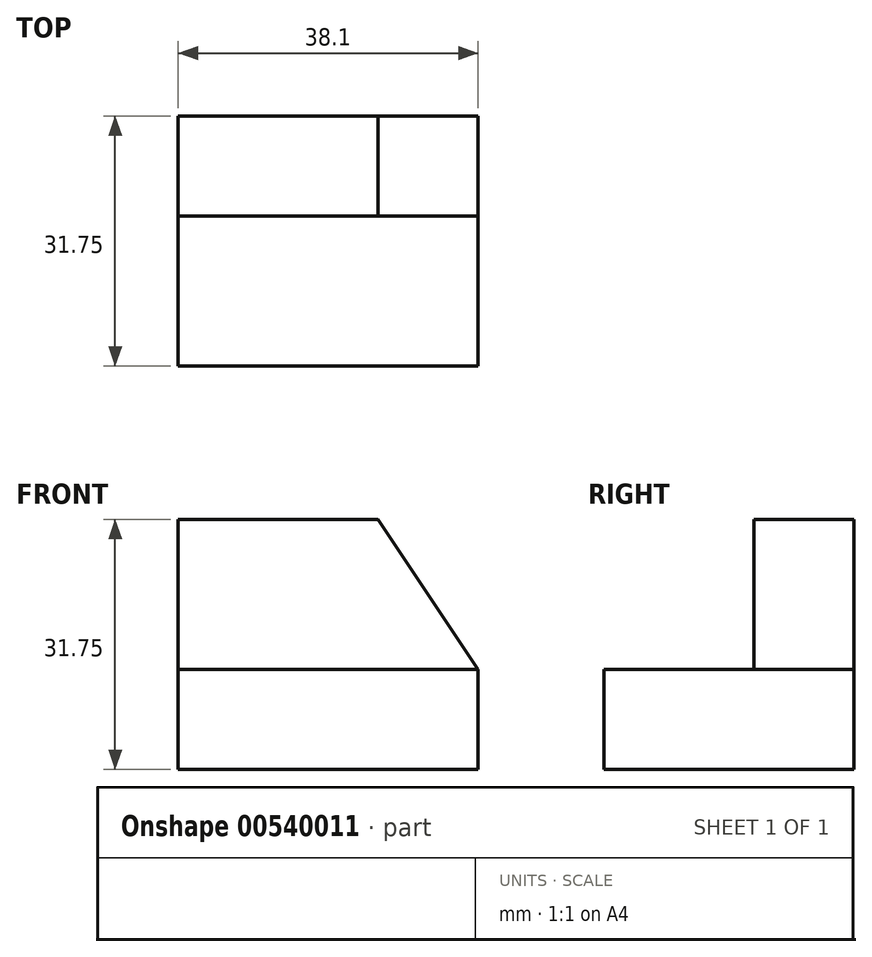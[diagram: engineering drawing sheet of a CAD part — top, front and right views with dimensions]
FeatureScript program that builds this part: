
annotation { "Feature Type Name" : "Feature", "Feature Type Description" : "" }
export const myFeature = defineFeature(function(context is Context, id is Id, definition is map)
    precondition{}
    {
        {
            var Q0;
            Q0=qCreatedBy(makeId("Right.planeOp"),FACE);
            var sketch = newSketch(context, id + "F0", { "sketchPlane" : qUnion([Q0])});
            skLineSegment(sketch, "E0", {"start": v(-47.28, 42.2) * mm, "end": v(-34.58, 42.2) * mm});
            skLineSegment(sketch, "E1", {"start": v(-47.28, 42.2) * mm, "end": v(-47.28, 23.16) * mm});
            skLineSegment(sketch, "E2", {"start": v(-47.28, 23.16) * mm, "end": v(-66.33, 23.16) * mm});
            skLineSegment(sketch, "E3", {"start": v(-66.33, 23.16) * mm, "end": v(-66.33, 10.46) * mm});
            skLineSegment(sketch, "E4", {"start": v(-66.33, 10.46) * mm, "end": v(-34.58, 10.46) * mm});
            skLineSegment(sketch, "E5", {"start": v(-34.58, 42.2) * mm, "end": v(-34.58, 10.46) * mm});
            skSolve(sketch);
        }
        {
            var Q0;
            Q0=makeQuery(id+"F0.imprint","IMPRINT",FACE,{"disambiguationData":[TD([[makeQuery(id+"F0.imprint","IMPRINT",EDGE,{"derivedFrom":sQuery(id+"F0.wireOp",EDGE,"E0")}),-1.0]])]});
            extrude(context, id + "F1", {"entities" : qUnion([Q0]), "depth" : 38.1 * mm, "offsetDistance" : 25.4 * mm});
        }
        {
            var Q0;
            Q0=makeQuery(id+"F1.opExtrude","SWEPT_FACE",FACE,{"disambiguationData":[OSD([sQuery(id+"F0.wireOp",EDGE,"E1")])]});
            var sketch = newSketch(context, id + "F2", { "sketchPlane" : qUnion([Q0])});
            skLineSegment(sketch, "E6", {"start": v(25.4, 42.2) * mm, "end": v(38.1, 23.16) * mm});
            skLineSegment(sketch, "E7", {"start": v(25.4, 42.2) * mm, "end": v(38.1, 42.2) * mm});
            skLineSegment(sketch, "E8", {"start": v(38.1, 42.2) * mm, "end": v(38.1, 23.16) * mm});
            skSolve(sketch);
        }
        {
            var Q0;
            Q0=makeQuery(id+"F2.imprint","IMPRINT",FACE,{"disambiguationData":[TD([[makeQuery(id+"F2.imprint","IMPRINT",EDGE,{"derivedFrom":sQuery(id+"F2.wireOp",EDGE,"E6")}),1.0]])]});
            extrude(context, id + "F3", {"entities" : qUnion([Q0]), "operationType" : NewBodyOperationType.REMOVE, "oppositeDirection" : true, "depth" : 25.4 * mm, "offsetDistance" : 25.4 * mm});
        }
    });
